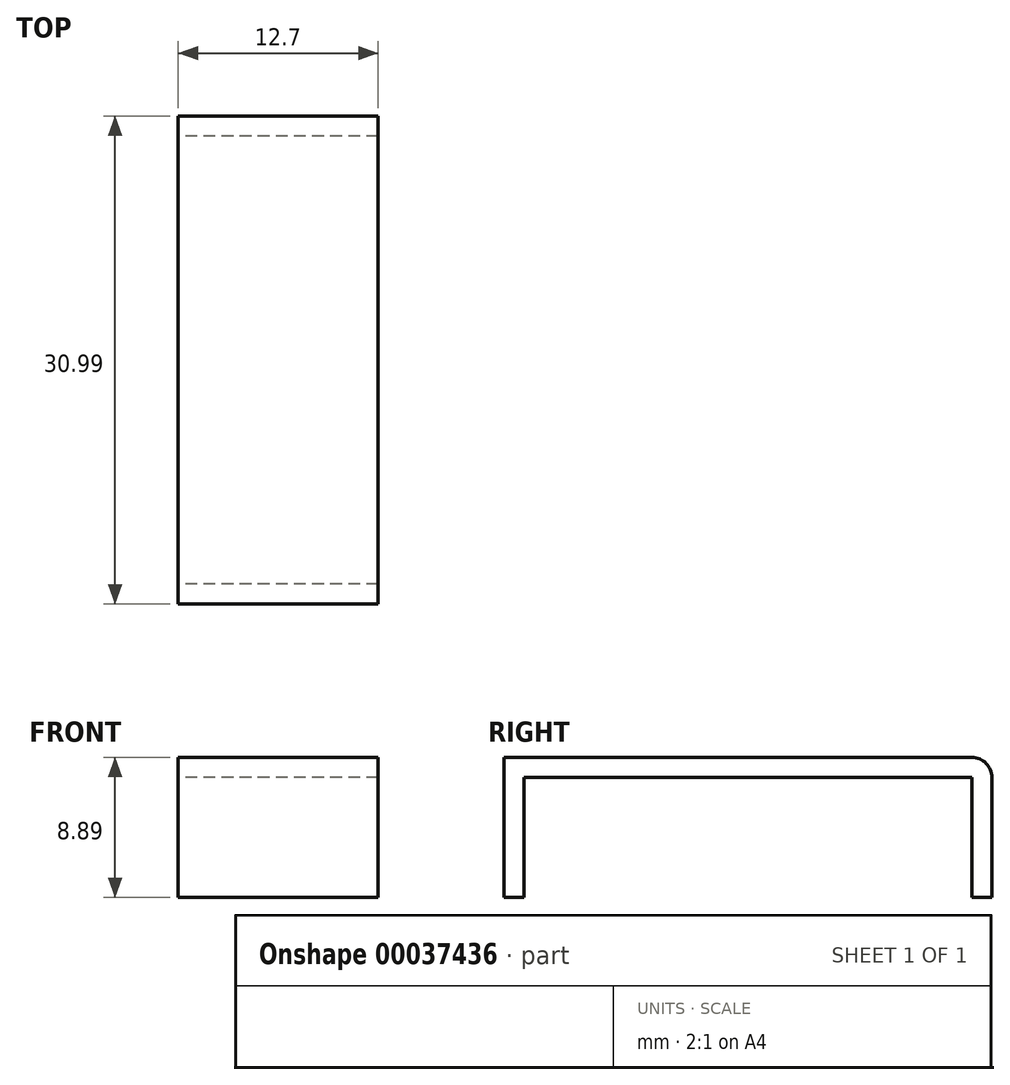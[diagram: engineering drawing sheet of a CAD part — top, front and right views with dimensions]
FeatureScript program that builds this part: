
annotation { "Feature Type Name" : "Feature", "Feature Type Description" : "" }
export const myFeature = defineFeature(function(context is Context, id is Id, definition is map)
    precondition{}
    {
        {
            var Q0;
            Q0=qCreatedBy(makeId("Top.planeOp"),FACE);
            var sketch = newSketch(context, id + "F0", { "sketchPlane" : qUnion([Q0])});
            skLineSegment(sketch, "E0.rect.bottom", {"start": v(0, -7.5) * mm, "end": v(-78.22, -7.5) * mm});
            skLineSegment(sketch, "E0.rect.top", {"start": v(0, 77.16) * mm, "end": v(-78.22, 77.16) * mm});
            skLineSegment(sketch, "E0.rect.left", {"start": v(0, -7.5) * mm, "end": v(0, 77.16) * mm});
            skLineSegment(sketch, "E0.rect.right", {"start": v(-78.22, -7.5) * mm, "end": v(-78.22, 77.16) * mm});
            skPoint(sketch, "E0.rect.middle", {"position": v(-39.1, 34.83) * mm});
            skSolve(sketch);
        }
        {
            var Q0;
            Q0=makeQuery(id+"F0.imprint","IMPRINT",FACE,{"disambiguationData":[TD([[makeQuery(id+"F0.imprint","IMPRINT",EDGE,{"derivedFrom":sQuery(id+"F0.wireOp",EDGE,"E0.rect.bottom")}),-1.0]])]});
            extrude(context, id + "F1", {"entities" : qUnion([Q0]), "depth" : 8.9 * mm});
        }
        {
            var Q0;
            Q0=makeQuery(id+"F1.opExtrude","SWEPT_FACE",FACE,{"disambiguationData":[OSD([sQuery(id+"F0.wireOp",EDGE,"E0.rect.bottom")])]});
            extrude(context, id + "F2", {"entities" : qUnion([Q0]), "operationType" : NewBodyOperationType.REMOVE, "oppositeDirection" : true, "depth" : 53.66 * mm});
        }
        {
            var Q0;
            Q0=makeQuery(id+"F1.opExtrude","SWEPT_FACE",FACE,{"disambiguationData":[OSD([sQuery(id+"F0.wireOp",EDGE,"E0.rect.left")])]});
            extrude(context, id + "F3", {"entities" : qUnion([Q0]), "operationType" : NewBodyOperationType.REMOVE, "oppositeDirection" : true, "depth" : 65.52 * mm});
        }
        {
            var Q0;
            Q0=makeQuery(id+"F3.boolean.opBoolean","COPY",FACE,{"derivedFrom":makeQuery(id+"F3.opExtrude","CAP_FACE",FACE,{"disambiguationData":[OSD([sQuery(id+"F0.wireOp",EDGE,"E0.rect.left")])],"isStart":false})});
            var Q1;
            Q1=makeQuery(id+"F1.opExtrude","SWEPT_BODY",BODY,{"disambiguationData":[OSD([sQuery(id+"F0.wireOp",EDGE,"E0.rect.bottom"),sQuery(id+"F0.wireOp",EDGE,"E0.rect.top"),sQuery(id+"F0.wireOp",EDGE,"E0.rect.left"),sQuery(id+"F0.wireOp",EDGE,"E0.rect.right")])]});
            shell(context, id + "F4", {"entities" : qUnion([Q0]), "parts" : qUnion([Q1]), "thickness" : 1.27 * mm});
        }
        {
            var Q0;
            {var subQ0=sQuery(id+"F0.wireOp",EDGE,"E0.rect.bottom");var subQ1=sQuery(id+"F0.wireOp",EDGE,"E0.rect.top");var subQ2=sQuery(id+"F0.wireOp",EDGE,"E0.rect.left");var subQ3=sQuery(id+"F0.wireOp",EDGE,"E0.rect.right");Q0=makeQuery(id+"F4.opShell","OFFSET_FACE",FACE,{"disambiguationData":[OSD([subQ0,subQ1,subQ2,subQ3]),TDD([makeQuery(id+"F1.opExtrude","CAP_FACE",FACE,{"disambiguationData":[OSD([subQ0,subQ1,subQ2,subQ3])],"isStart":true})])]});}
            extrude(context, id + "F5", {"entities" : qUnion([Q0]), "operationType" : NewBodyOperationType.REMOVE, "oppositeDirection" : true, "depth" : 25.4 * mm});
        }
        {
            var Q0;
            {var subQ0=sQuery(id+"F0.wireOp",EDGE,"E0.rect.right");Q0=makeQuery(id+"F5.boolean.opBoolean","MERGE",FACE,{"derivedFrom":[makeQuery(id+"F4.opShell","OFFSET_FACE",FACE,{"disambiguationData":[OSD([subQ0])]}),makeQuery(id+"F5.opExtrude","SWEPT_FACE",FACE,{"disambiguationData":[OSD([subQ0])]})]});}
            extrude(context, id + "F6", {"entities" : qUnion([Q0]), "operationType" : NewBodyOperationType.REMOVE, "oppositeDirection" : true, "depth" : 25.4 * mm});
        }
        {
            var Q0;
            {var subQ0=sQuery(id+"F0.wireOp",EDGE,"E0.rect.bottom");Q0=makeQuery(id+"F2.boolean.opBoolean","COPY",EDGE,{"derivedFrom":makeQuery(id+"F2.opExtrude","CAP_EDGE",EDGE,{"disambiguationData":[OSD([subQ0]),TDD([makeQuery(id+"F1.opExtrude","CAP_EDGE",EDGE,{"disambiguationData":[OSD([subQ0])],"isStart":false})])],"isStart":false})});}
            var Q1;
            Q1=makeQuery(id+"F1.opExtrude","CAP_EDGE",EDGE,{"disambiguationData":[OSD([sQuery(id+"F0.wireOp",EDGE,"E0.rect.top")])],"isStart":false});
            fillet(context, id + "F7", {"entities" : qUnion([Q0, Q1]), "radius" : 1.27 * mm, "tangentPropagation" : true, "allowEdgeOverflow" : false});
        }
    });
